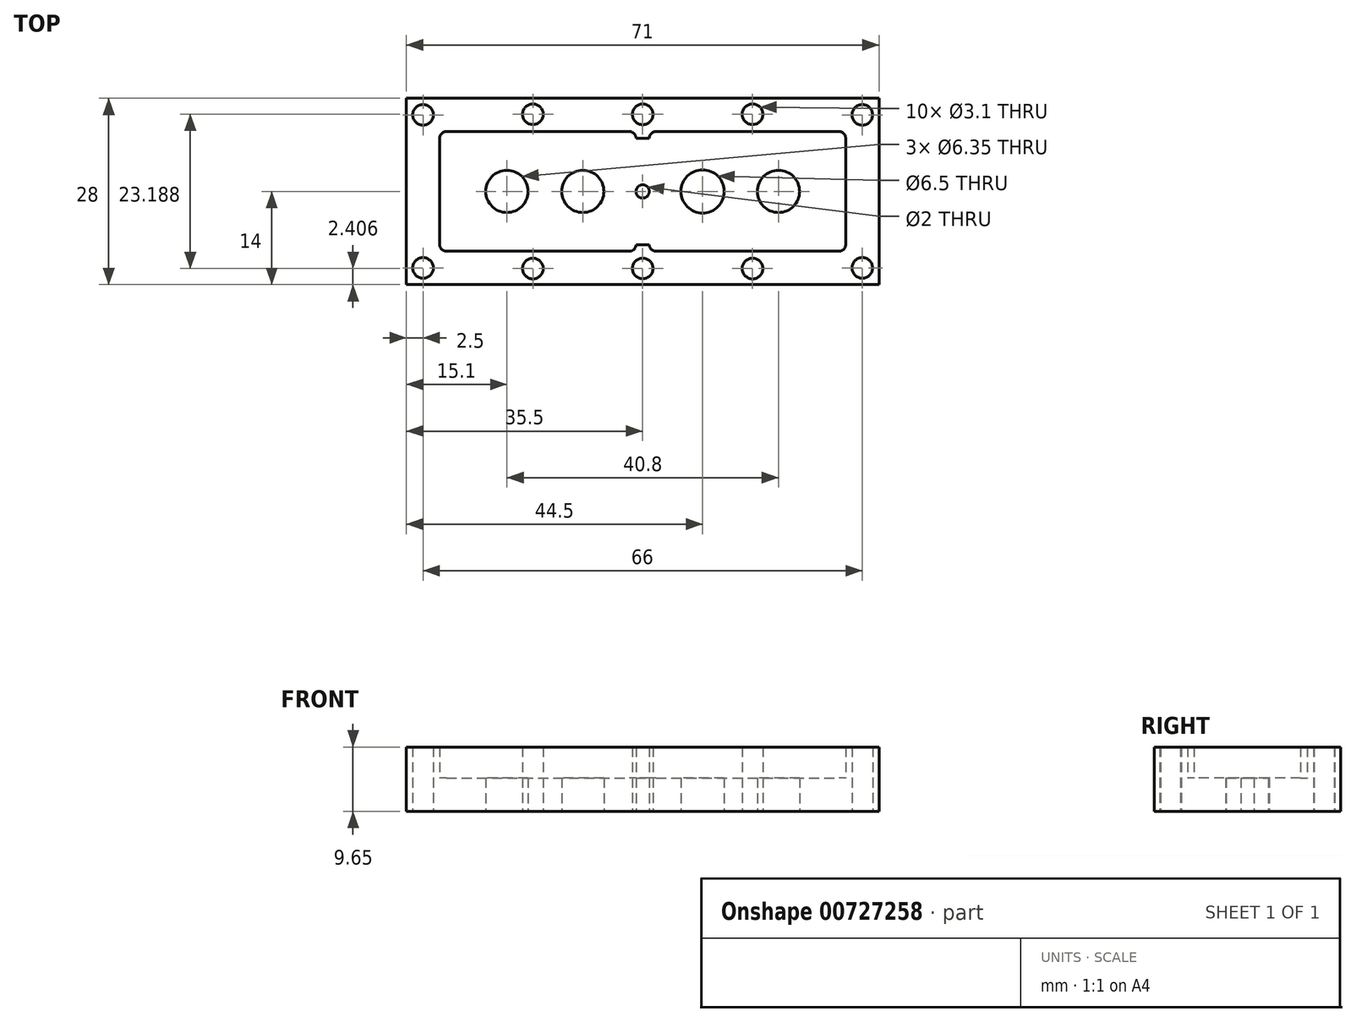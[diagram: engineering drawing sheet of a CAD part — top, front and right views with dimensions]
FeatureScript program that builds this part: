
annotation { "Feature Type Name" : "Feature", "Feature Type Description" : "" }
export const myFeature = defineFeature(function(context is Context, id is Id, definition is map)
    precondition{}
    {
        {
            var Q0;
            Q0=qCreatedBy(makeId("Top.planeOp"),FACE);
            var sketch = newSketch(context, id + "F0", { "sketchPlane" : qUnion([Q0])});
            skLineSegment(sketch, "E0.bottom", {"start": v(-35.5, 14) * mm, "end": v(35.5, 14) * mm});
            skLineSegment(sketch, "E0.top", {"start": v(-35.5, -14) * mm, "end": v(35.5, -14) * mm});
            skLineSegment(sketch, "E0.left", {"start": v(-35.5, 14) * mm, "end": v(-35.5, -14) * mm});
            skLineSegment(sketch, "E0.right", {"start": v(35.5, 14) * mm, "end": v(35.5, -14) * mm});
            skPoint(sketch, "E0.middle", {"position": v(0, 0) * mm});
            skLineSegment(sketch, "E1.bottom", {"start": v(-30.5, 9) * mm, "end": v(30.5, 9) * mm});
            skLineSegment(sketch, "E1.top", {"start": v(-30.5, -9) * mm, "end": v(30.5, -9) * mm});
            skLineSegment(sketch, "E1.left", {"start": v(-30.5, 9) * mm, "end": v(-30.5, -9) * mm});
            skLineSegment(sketch, "E1.right", {"start": v(30.5, 9) * mm, "end": v(30.5, -9) * mm});
            skCircle(sketch, "E2", {"center": v(-20.4, 0) * mm, "radius": 3.17 * mm});
            skCircle(sketch, "E3", {"center": v(-9, 0) * mm, "radius": 3.17 * mm});
            skCircle(sketch, "E4", {"center": v(20.4, 0) * mm, "radius": 3.17 * mm});
            skCircle(sketch, "E5", {"center": v(9, 0) * mm, "radius": 3.25 * mm});
            skCircle(sketch, "E6", {"center": v(0, 0) * mm, "radius": 1 * mm});
            skCircle(sketch, "E7", {"center": v(-33, 11.5) * mm, "radius": 1.55 * mm});
            skCircle(sketch, "E8", {"center": v(-16.5, 11.6) * mm, "radius": 1.55 * mm});
            skCircle(sketch, "E9", {"center": v(0, 11.58) * mm, "radius": 1.55 * mm});
            skCircle(sketch, "E10.MirrorC", {"center": v(-33, -11.5) * mm, "radius": 1.55 * mm});
            skCircle(sketch, "E11.MirrorC", {"center": v(33, 11.5) * mm, "radius": 1.55 * mm});
            skCircle(sketch, "E12.MirrorC", {"center": v(33, -11.5) * mm, "radius": 1.55 * mm});
            skCircle(sketch, "E13.MirrorC", {"center": v(-16.5, -11.6) * mm, "radius": 1.55 * mm});
            skCircle(sketch, "E14.MirrorC", {"center": v(16.5, 11.6) * mm, "radius": 1.55 * mm});
            skCircle(sketch, "E15.MirrorC", {"center": v(16.5, -11.6) * mm, "radius": 1.55 * mm});
            skCircle(sketch, "E16.MirrorC", {"center": v(0, -11.58) * mm, "radius": 1.55 * mm});
            skLineSegment(sketch, "E17.bottom", {"start": v(-1, -9) * mm, "end": v(1, -9) * mm});
            skLineSegment(sketch, "E17.top", {"start": v(-1, 9) * mm, "end": v(1, 9) * mm});
            skLineSegment(sketch, "E17.left", {"start": v(-1, -9) * mm, "end": v(-1, 9) * mm});
            skLineSegment(sketch, "E17.right", {"start": v(1, -9) * mm, "end": v(1, 9) * mm});
            skLineSegment(sketch, "E18.top", {"start": v(-1, -8) * mm, "end": v(1, -8) * mm});
            skLineSegment(sketch, "E18.left", {"start": v(-1, -9) * mm, "end": v(-1, -8) * mm});
            skLineSegment(sketch, "E18.right", {"start": v(1, -9) * mm, "end": v(1, -8) * mm});
            skLineSegment(sketch, "E19.top", {"start": v(-1, 8) * mm, "end": v(1, 8) * mm});
            skLineSegment(sketch, "E19.left", {"start": v(-1, 9) * mm, "end": v(-1, 8) * mm});
            skLineSegment(sketch, "E19.right", {"start": v(1, 9) * mm, "end": v(1, 8) * mm});
            skSolve(sketch);
        }
        {
            var Q0;
            Q0=makeQuery(id+"F0.imprint","IMPRINT",FACE,{"disambiguationData":[TD([[makeQuery(id+"F0.imprint","IMPRINT",EDGE,{"derivedFrom":sQuery(id+"F0.wireOp",EDGE,"E0.bottom")}),-1.0]])]});
            var Q1;
            {var subQ5=sQuery(id+"F0.wireOp",EDGE,"E18.top");Q1=makeQuery(id+"F0.imprint","IMPRINT",FACE,{"disambiguationData":[TD([[makeQuery(id+"F0.imprint","IMPRINT",EDGE,{"derivedFrom":subQ5}),-1.0]])]});}
            var Q2;
            {var subQ5=sQuery(id+"F0.wireOp",EDGE,"E19.top");Q2=makeQuery(id+"F0.imprint","IMPRINT",FACE,{"disambiguationData":[TD([[makeQuery(id+"F0.imprint","IMPRINT",EDGE,{"derivedFrom":subQ5}),1.0]])]});}
            extrude(context, id + "F1", {"entities" : qUnion([Q0, Q1, Q2]), "depth" : (5 + 10 - 5.35) * mm, "offsetDistance" : 25 * mm});
        }
        {
            var Q0;
            {var subQ0=sQuery(id+"F0.wireOp",EDGE,"E1.right");Q0=makeQuery(id+"F0.imprint","IMPRINT",FACE,{"disambiguationData":[TD([[makeQuery(id+"F0.imprint","IMPRINT",EDGE,{"derivedFrom":subQ0}),-1.0]])]});}
            var Q1;
            {var subQ0=sQuery(id+"F0.wireOp",EDGE,"E1.left");Q1=makeQuery(id+"F0.imprint","IMPRINT",FACE,{"disambiguationData":[TD([[makeQuery(id+"F0.imprint","IMPRINT",EDGE,{"derivedFrom":subQ0}),1.0]])]});}
            var Q2;
            {var subQ5=sQuery(id+"F0.wireOp",EDGE,"E18.top");Q2=makeQuery(id+"F0.imprint","IMPRINT",FACE,{"disambiguationData":[TD([[makeQuery(id+"F0.imprint","IMPRINT",EDGE,{"derivedFrom":subQ5}),1.0]])]});}
            var Q3;
            {var subQ5=sQuery(id+"F0.wireOp",EDGE,"E19.top");Q3=makeQuery(id+"F0.imprint","IMPRINT",FACE,{"disambiguationData":[TD([[makeQuery(id+"F0.imprint","IMPRINT",EDGE,{"derivedFrom":subQ5}),-1.0]])]});}
            extrude(context, id + "F2", {"entities" : qUnion([Q0, Q1, Q2, Q3]), "operationType" : NewBodyOperationType.ADD, "depth" : 5 * mm, "offsetDistance" : 25 * mm});
        }
        {
            var Q0;
            Q0=makeQuery(id+"F1.opExtrude","SWEPT_EDGE",EDGE,{"disambiguationData":[OSD([sQuery(id+"F0.wireOp",EDGE,"E1.top"),sQuery(id+"F0.wireOp",EDGE,"E1.left")])]});
            var Q1;
            Q1=makeQuery(id+"F1.opExtrude","SWEPT_EDGE",EDGE,{"disambiguationData":[OSD([sQuery(id+"F0.wireOp",EDGE,"E1.top"),sQuery(id+"F0.wireOp",EDGE,"E17.left")])]});
            var Q2;
            Q2=makeQuery(id+"F1.opExtrude","SWEPT_EDGE",EDGE,{"disambiguationData":[OSD([sQuery(id+"F0.wireOp",EDGE,"E1.bottom"),sQuery(id+"F0.wireOp",EDGE,"E1.left")])]});
            var Q3;
            Q3=makeQuery(id+"F1.opExtrude","SWEPT_EDGE",EDGE,{"disambiguationData":[OSD([sQuery(id+"F0.wireOp",EDGE,"E1.bottom"),sQuery(id+"F0.wireOp",EDGE,"E17.left")])]});
            var Q4;
            Q4=makeQuery(id+"F1.opExtrude","SWEPT_EDGE",EDGE,{"disambiguationData":[OSD([sQuery(id+"F0.wireOp",EDGE,"E1.bottom"),sQuery(id+"F0.wireOp",EDGE,"E17.right")])]});
            var Q5;
            Q5=makeQuery(id+"F1.opExtrude","SWEPT_EDGE",EDGE,{"disambiguationData":[OSD([sQuery(id+"F0.wireOp",EDGE,"E1.top"),sQuery(id+"F0.wireOp",EDGE,"E17.right")])]});
            var Q6;
            Q6=makeQuery(id+"F1.opExtrude","SWEPT_EDGE",EDGE,{"disambiguationData":[OSD([sQuery(id+"F0.wireOp",EDGE,"E1.top"),sQuery(id+"F0.wireOp",EDGE,"E1.right")])]});
            var Q7;
            Q7=makeQuery(id+"F1.opExtrude","SWEPT_EDGE",EDGE,{"disambiguationData":[OSD([sQuery(id+"F0.wireOp",EDGE,"E1.bottom"),sQuery(id+"F0.wireOp",EDGE,"E1.right")])]});
            fillet(context, id + "F3", {"entities" : qUnion([Q0, Q1, Q2, Q3, Q4, Q5, Q6, Q7]), "radius" : 1 * mm, "tangentPropagation" : true, "defaultsChanged" : false, "vertexSettings" : [], "allowEdgeOverflow" : false});
        }
    });
